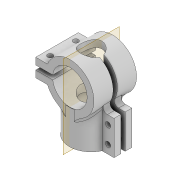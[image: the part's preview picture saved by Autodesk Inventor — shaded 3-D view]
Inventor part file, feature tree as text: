
AUTODESK INVENTOR PART (.ipt)
format: ipt  version: 2022 (Build 260153000, 153)  size: 337,920 bytes
history: native  units: mm
features: extrude x5, sketch x4, fillet x1
ambient origin geometry x8: Origin, YZ Plane, XZ Plane, XY Plane, X Axis, Y Axis, Z Axis, Center Point
bodies: Solid1 (feature_tree)
feature tree (10):
  sketch  "Sketch1"  dims[d0=35.0mm d1=8.0mm]
  extrude  "Extrusion1"  Depth=8.0mm
  extrude  "Extrusion4"  Depth=8.0mm
  extrude  "Extrusion5"  Depth=2.5mm
  fillet  "Fillet1"  Radius=20.0mm
  extrude  "Extrusion6"  Depth=10.0mm TaperAngle=0.0deg
  extrude  "Extrusion7"  Depth=10.0mm
  sketch  "Sketch4"  dims[d2=8.0mm d3=8.0mm]
  sketch  "Sketch5"  dims[d7=2.5mm d8=2.5mm d9=20.0mm]
  sketch  "Sketch6"  dims[d10=20.0mm d11=40.0mm d12=0.0mm d24=40.5mm d25=8.0mm d26=8.0mm d27=8.0mm d28=20.0mm d29=20.0mm d30=2.5mm d31=50.0mm d32=0.0mm d33=100.0mm d34=0.0mm d35=25.0mm d36=5.0mm d37=6.2mm d38=6.2mm d39=10.0mm d40=10.0mm d41=7.0mm d42=7.0mm d43=100.0mm d44=0.0mm d45=6.2mm d46=6.2mm d47=7.0mm d48=7.0mm d49=10.0mm d50=10.0mm d51=100.0mm d52=0.0mm]
